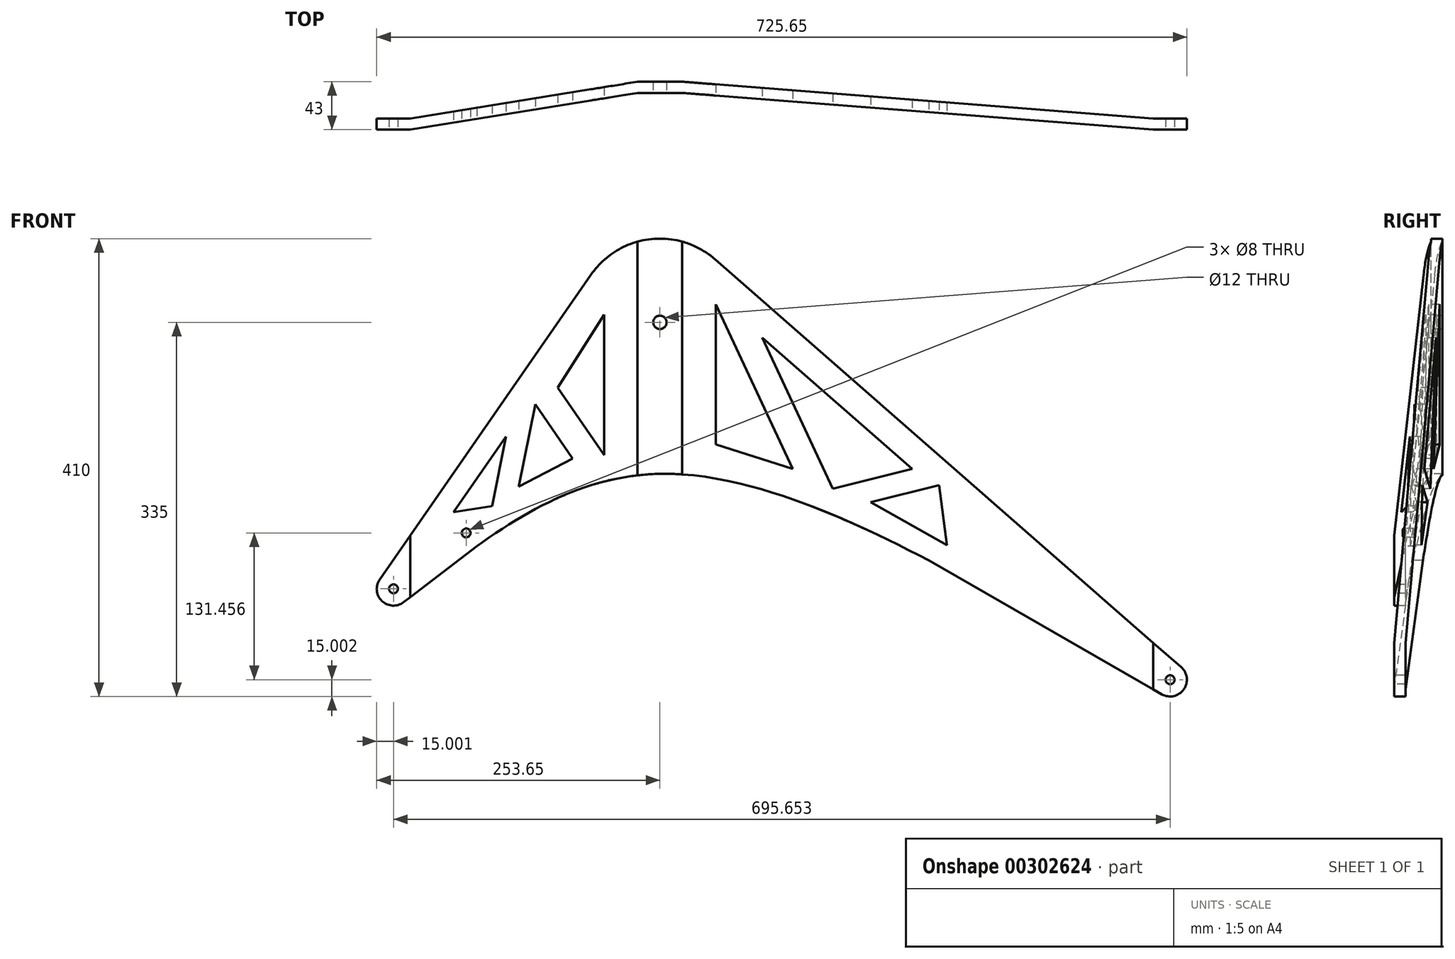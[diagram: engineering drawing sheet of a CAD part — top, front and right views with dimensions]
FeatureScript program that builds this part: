
annotation { "Feature Type Name" : "Feature", "Feature Type Description" : "" }
export const myFeature = defineFeature(function(context is Context, id is Id, definition is map)
    precondition{}
    {
        {
            var Q0;
            Q0=qCreatedBy(makeId("Front.planeOp"),FACE);
            var sketch = newSketch(context, id + "F0", { "sketchPlane" : qUnion([Q0])});
            skCircle(sketch, "E0", {"center": v(0, 0) * mm, "radius": 5 * mm});
            skCircle(sketch, "E1", {"center": v(-238.65, -238.65) * mm, "radius": 4 * mm});
            skCircle(sketch, "E2", {"center": v(457, -320) * mm, "radius": 4 * mm});
            skLineSegment(sketch, "E3", {"start": v(-238.65, -238.65) * mm, "end": v(0, 0) * mm});
            skLineSegment(sketch, "E4", {"start": v(0, 0) * mm, "end": v(457, -320) * mm});
            skLineSegment(sketch, "E5", {"start": v(0, 0) * mm, "end": v(0, -238.65) * mm});
            skLineSegment(sketch, "E6", {"start": v(0, -238.65) * mm, "end": v(-238.65, -238.65) * mm});
            skLineSegment(sketch, "E7", {"start": v(0, -238.65) * mm, "end": v(0, -320) * mm});
            skLineSegment(sketch, "E8", {"start": v(0, -320) * mm, "end": v(457, -320) * mm});
            skSolve(sketch);
        }
        {
            var Q0;
            Q0=qCreatedBy(makeId("Top.planeOp"),FACE);
            var sketch = newSketch(context, id + "F1", { "sketchPlane" : qUnion([Q0])});
            skLineSegment(sketch, "E9.bottom", {"start": v(-20, 0) * mm, "end": v(20, 0) * mm});
            skLineSegment(sketch, "E9.top", {"start": v(-20, -10) * mm, "end": v(20, -10) * mm});
            skLineSegment(sketch, "E9.left", {"start": v(-20, 0) * mm, "end": v(-20, -10) * mm});
            skLineSegment(sketch, "E9.right", {"start": v(20, 0) * mm, "end": v(20, -10) * mm});
            skLineSegment(sketch, "E10", {"start": v(472, -43) * mm, "end": v(472, -33) * mm});
            skLineSegment(sketch, "E11", {"start": v(-253.65, -43) * mm, "end": v(-253.65, -33) * mm});
            skLineSegment(sketch, "E12", {"start": v(472, -33) * mm, "end": v(442, -33) * mm});
            skLineSegment(sketch, "E13", {"start": v(442, -33) * mm, "end": v(442, -43) * mm});
            skLineSegment(sketch, "E14", {"start": v(442, -43) * mm, "end": v(472, -43) * mm});
            skLineSegment(sketch, "E15", {"start": v(-253.65, -33) * mm, "end": v(-223.65, -33) * mm});
            skLineSegment(sketch, "E16", {"start": v(-223.65, -33) * mm, "end": v(-223.65, -43) * mm});
            skLineSegment(sketch, "E17", {"start": v(-223.65, -43) * mm, "end": v(-253.65, -43) * mm});
            skLineSegment(sketch, "E18", {"start": v(-223.65, -43) * mm, "end": v(-20, -10) * mm});
            skLineSegment(sketch, "E19", {"start": v(-20, 0) * mm, "end": v(-223.65, -33) * mm});
            skLineSegment(sketch, "E20", {"start": v(20, 0) * mm, "end": v(442, -33) * mm});
            skLineSegment(sketch, "E21", {"start": v(442, -43) * mm, "end": v(20, -10) * mm});
            skLineSegment(sketch, "E22", {"start": v(0, 0) * mm, "end": v(0, 130) * mm});
            skLineSegment(sketch, "E23", {"start": v(0, 65) * mm, "end": v(-332.58, 65) * mm});
            skLineSegment(sketch, "E24", {"start": v(0, -10) * mm, "end": v(0, -75) * mm});
            skPoint(sketch, "E24.endSnap0", {"position": v(0, -10) * mm});
            skSolve(sketch);
        }
        {
            var Q0;
            Q0=qSketchRegion(id+"F1",true);
            extrude(context, id + "F2", {"entities" : qUnion([Q0]), "oppositeDirection" : true, "depth" : 340 * mm});
        }
        {
            var Q0;
            Q0=qSketchRegion(id+"F1",true);
            extrude(context, id + "F3", {"entities" : qUnion([Q0]), "operationType" : NewBodyOperationType.ADD, "depth" : 100 * mm});
        }
        {
            var Q0;
            Q0=qCreatedBy(makeId("Front.planeOp"),FACE);
            var sketch = newSketch(context, id + "F4", { "sketchPlane" : qUnion([Q0])});
            skCircle(sketch, "E25", {"center": v(-238.65, -238.65) * mm, "radius": 15 * mm});
            skCircle(sketch, "E26", {"center": v(457, -320) * mm, "radius": 15 * mm});
            skCircle(sketch, "E27", {"center": v(0, 0) * mm, "radius": 75 * mm});
            skLineSegment(sketch, "E28", {"start": v(-264.4, -249.44) * mm, "end": v(-11, 115.7) * mm});
            skLineSegment(sketch, "E29", {"start": v(12.3, 88.89) * mm, "end": v(551.26, -382.5) * mm});
            skLineSegment(sketch, "E30", {"start": v(0, -75) * mm, "end": v(-229.54, -250.56) * mm});
            skLineSegment(sketch, "E31", {"start": v(0, -75) * mm, "end": v(449.54, -333) * mm});
            skFitSpline(sketch, "E32", {"points": [v(-229.54, -250.56) * mm, v(0, -135.64) * mm, v(449.54, -333) * mm], "startDerivative": vector(454.74, 347.81) * mm, "endDerivative": vector(744.11, -427.08) * mm});
            skSolve(sketch);
        }
        {
            var Q0;
            Q0=qSketchRegion(id+"F4",true);
            extrude(context, id + "F5", {"entities" : qUnion([Q0]), "operationType" : NewBodyOperationType.INTERSECT, "endBound" : BoundingType.SYMMETRIC, "oppositeDirection" : true, "depth" : 152 * mm});
        }
        {
            var Q0;
            {var subQ0=sQuery(id+"F1.wireOp",EDGE,"E9.top");Q0=makeQuery(id+"F3.boolean.opBoolean","MERGE",FACE,{"derivedFrom":[makeQuery(id+"F2.opExtrude","SWEPT_FACE",FACE,{"disambiguationData":[OSD([subQ0])]}),makeQuery(id+"F3.opExtrude","SWEPT_FACE",FACE,{"disambiguationData":[OSD([subQ0])]})]});}
            var sketch = newSketch(context, id + "F6", { "sketchPlane" : qUnion([Q0])});
            skLineSegment(sketch, "E33", {"start": v(-50, 6.88) * mm, "end": v(-50, -118.87) * mm});
            skLineSegment(sketch, "E34", {"start": v(-50, -118.87) * mm, "end": v(-91.57, -58.59) * mm});
            skLineSegment(sketch, "E35", {"start": v(-91.57, -58.59) * mm, "end": v(-50, 6.88) * mm});
            skLineSegment(sketch, "E36", {"start": v(-78.26, -121.92) * mm, "end": v(-111.7, -73.42) * mm});
            skLineSegment(sketch, "E37", {"start": v(-111.7, -73.42) * mm, "end": v(-126.47, -146.98) * mm});
            skLineSegment(sketch, "E38", {"start": v(-126.47, -146.98) * mm, "end": v(-78.26, -121.92) * mm});
            skLineSegment(sketch, "E39", {"start": v(-137.89, -102.22) * mm, "end": v(-150.41, -164.65) * mm});
            skLineSegment(sketch, "E40", {"start": v(-184.86, -169.92) * mm, "end": v(-137.89, -102.22) * mm});
            skLineSegment(sketch, "E41", {"start": v(50, -109.34) * mm, "end": v(50, 16.05) * mm});
            skLineSegment(sketch, "E42", {"start": v(50, 16.05) * mm, "end": v(118.97, -131.23) * mm});
            skLineSegment(sketch, "E43", {"start": v(118.97, -131.23) * mm, "end": v(50, -109.34) * mm});
            skLineSegment(sketch, "E44", {"start": v(91.49, -13.6) * mm, "end": v(154.91, -149.03) * mm});
            skLineSegment(sketch, "E45", {"start": v(154.91, -149.03) * mm, "end": v(225.97, -131.22) * mm});
            skLineSegment(sketch, "E46", {"start": v(225.97, -131.22) * mm, "end": v(91.49, -13.6) * mm});
            skLineSegment(sketch, "E47", {"start": v(188.86, -161.14) * mm, "end": v(250.2, -145.76) * mm});
            skLineSegment(sketch, "E48", {"start": v(250.2, -145.76) * mm, "end": v(257, -199.36) * mm});
            skLineSegment(sketch, "E49", {"start": v(257, -199.36) * mm, "end": v(188.86, -161.14) * mm});
            skLineSegment(sketch, "E50", {"start": v(-184.86, -169.92) * mm, "end": v(-150.41, -164.65) * mm});
            skCircle(sketch, "E51", {"center": v(-238.65, -238.65) * mm, "radius": 4 * mm});
            skCircle(sketch, "E52", {"center": v(457, -320) * mm, "radius": 4 * mm});
            skCircle(sketch, "E53", {"center": v(0, 0) * mm, "radius": 6 * mm});
            skCircle(sketch, "E54", {"center": v(-173.55, -188.54) * mm, "radius": 4 * mm});
            skSolve(sketch);
        }
        {
            var Q0;
            Q0=qSketchRegion(id+"F6",true);
            extrude(context, id + "F7", {"entities" : qUnion([Q0]), "operationType" : NewBodyOperationType.REMOVE, "endBound" : BoundingType.SYMMETRIC, "oppositeDirection" : true, "depth" : 132 * mm});
        }
    });
